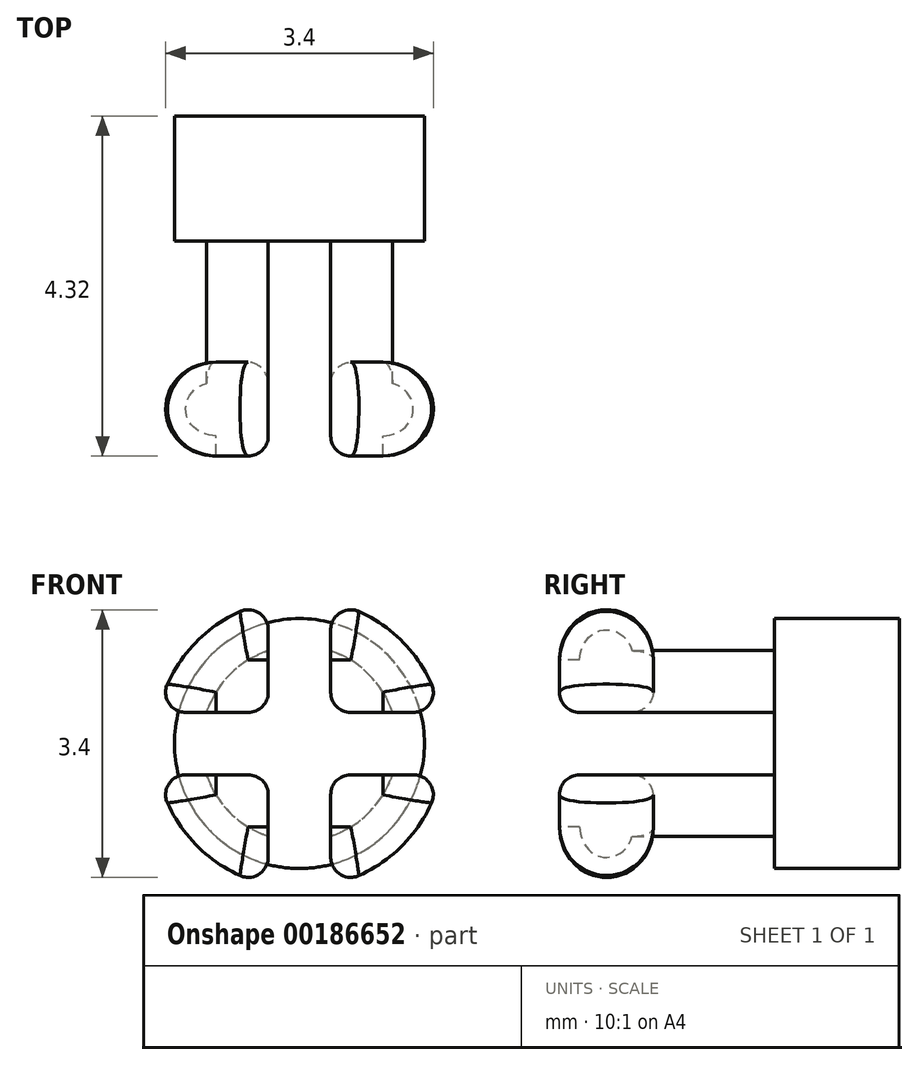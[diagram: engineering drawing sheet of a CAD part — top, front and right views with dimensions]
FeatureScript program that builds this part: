
annotation { "Feature Type Name" : "Feature", "Feature Type Description" : "" }
export const myFeature = defineFeature(function(context is Context, id is Id, definition is map)
    precondition{}
    {
        {
            var Q0;
            Q0=qCreatedBy(makeId("Front.planeOp"),FACE);
            var sketch = newSketch(context, id + "F0", { "sketchPlane" : qUnion([Q0])});
            skCircle(sketch, "E0", {"center": v(0, 0) * mm, "radius": 1.59 * mm});
            skSolve(sketch);
        }
        {
            var Q0;
            Q0=makeQuery(id+"F0.imprint","IMPRINT",FACE,{"disambiguationData":[TD([[makeQuery(id+"F0.imprint","IMPRINT",EDGE,{"derivedFrom":sQuery(id+"F0.wireOp",EDGE,"E0")}),1.0]])]});
            extrude(context, id + "F1", {"entities" : qUnion([Q0]), "depth" : 1.59 * mm});
        }
        {
            var Q0;
            Q0=makeQuery(id+"F1.opExtrude","CAP_FACE",FACE,{"disambiguationData":[OSD([sQuery(id+"F0.wireOp",EDGE,"E0")])],"isStart":false});
            var sketch = newSketch(context, id + "F2", { "sketchPlane" : qUnion([Q0])});
            skCircle(sketch, "E1", {"center": v(0, 0) * mm, "radius": 1.24 * mm});
            skSolve(sketch);
        }
        {
            var Q0;
            Q0=makeQuery(id+"F2.imprint","IMPRINT",FACE,{"disambiguationData":[TD([[makeQuery(id+"F2.imprint","IMPRINT",EDGE,{"derivedFrom":sQuery(id+"F2.wireOp",EDGE,"E1")}),1.0]])]});
            extrude(context, id + "F3", {"entities" : qUnion([Q0]), "operationType" : NewBodyOperationType.ADD, "depth" : 2.73 * mm});
        }
        {
            var Q0;
            Q0=qCreatedBy(makeId("Right.planeOp"),FACE);
            var sketch = newSketch(context, id + "F4", { "sketchPlane" : qUnion([Q0])});
            skLineSegment(sketch, "E2.bottom", {"start": v(-4.32, 0) * mm, "end": v(-3.12, 0) * mm, "construction": true});
            skLineSegment(sketch, "E2.top", {"start": v(-4.32, -1.24) * mm, "end": v(-3.12, -1.24) * mm, "construction": true});
            skLineSegment(sketch, "E2.left", {"start": v(-4.32, 0) * mm, "end": v(-4.32, -1.24) * mm, "construction": true});
            skLineSegment(sketch, "E2.right", {"start": v(-3.12, 0) * mm, "end": v(-3.12, -1.24) * mm, "construction": true});
            skArc(sketch, "E3", {"start": v(-4.32, -1.24) * mm, "mid": v(-3.72, -1.84) * mm, "end": v(-3.12, -1.24) * mm});
            skLineSegment(sketch, "E4", {"start": v(-4.32, -1.24) * mm, "end": v(-3.12, -1.24) * mm});
            skSolve(sketch);
        }
        {
            var Q0;
            Q0 = qSketchRegion(id + "F4", true);
            var Q1;
            Q1=sQuery(id+"F4.wireOp",EDGE,"E2.bottom");
            revolve(context, id + "F5", {"operationType" : NewBodyOperationType.ADD, "entities" : qUnion([Q0]), "axis" : qUnion([Q1]), "revolveType" : RevolveType.FULL});
        }
        {
            var Q0;
            Q0=makeQuery(id+"F3.opExtrude","CAP_FACE",FACE,{"disambiguationData":[OSD([sQuery(id+"F2.wireOp",EDGE,"E1")])],"isStart":false});
            var sketch = newSketch(context, id + "F6", { "sketchPlane" : qUnion([Q0])});
            skLineSegment(sketch, "E5.bottom", {"start": v(0.4, 2.76) * mm, "end": v(-0.4, 2.76) * mm});
            skLineSegment(sketch, "E5.top", {"start": v(0.4, -2.76) * mm, "end": v(-0.4, -2.76) * mm});
            skLineSegment(sketch, "E5.left", {"start": v(0.4, 2.76) * mm, "end": v(0.4, -2.76) * mm});
            skLineSegment(sketch, "E5.right", {"start": v(-0.4, 2.76) * mm, "end": v(-0.4, -2.76) * mm});
            skPoint(sketch, "E5.middle", {"position": v(0, 0) * mm});
            skLineSegment(sketch, "E6.bottom", {"start": v(2.76, -0.4) * mm, "end": v(-2.76, -0.4) * mm});
            skLineSegment(sketch, "E6.top", {"start": v(2.76, 0.4) * mm, "end": v(-2.76, 0.4) * mm});
            skLineSegment(sketch, "E6.left", {"start": v(2.76, -0.4) * mm, "end": v(2.76, 0.4) * mm});
            skLineSegment(sketch, "E6.right", {"start": v(-2.76, -0.4) * mm, "end": v(-2.76, 0.4) * mm});
            skSolve(sketch);
        }
        {
            var Q0;
            {var subQ0=sQuery(id+"F6.wireOp",EDGE,"E5.bottom");Q0=makeQuery(id+"F6.imprint","IMPRINT",FACE,{"disambiguationData":[TD([[makeQuery(id+"F6.imprint","IMPRINT",EDGE,{"derivedFrom":subQ0}),1.0]])]});}
            var Q1;
            {var subQ0=sQuery(id+"F6.wireOp",EDGE,"E6.top");var subQ1=sQuery(id+"F6.wireOp",EDGE,"E5.left");var subQ2=makeQuery(id+"F6.imprint","INTERSECT",VERTEX,{"derivedFrom":[subQ1,subQ0]});Q1=makeQuery(id+"F6.imprint","IMPRINT",FACE,{"disambiguationData":[TD([[makeQuery(id+"F6.imprint","IMPRINT",EDGE,{"disambiguationData":[TD([[subQ2,-1.0]])],"derivedFrom":subQ0}),-1.0]])]});}
            var Q2;
            {var subQ0=sQuery(id+"F6.wireOp",EDGE,"E6.top");var subQ1=sQuery(id+"F6.wireOp",EDGE,"E5.left");var subQ2=makeQuery(id+"F6.imprint","INTERSECT",VERTEX,{"derivedFrom":[subQ1,subQ0]});Q2=makeQuery(id+"F6.imprint","IMPRINT",FACE,{"disambiguationData":[TD([[makeQuery(id+"F6.imprint","IMPRINT",EDGE,{"disambiguationData":[TD([[subQ2,-1.0]])],"derivedFrom":subQ1}),-1.0]])]});}
            var Q3;
            {var subQ0=sQuery(id+"F6.wireOp",EDGE,"E6.bottom");var subQ1=sQuery(id+"F6.wireOp",EDGE,"E5.left");var subQ2=makeQuery(id+"F6.imprint","INTERSECT",VERTEX,{"derivedFrom":[subQ1,subQ0]});Q3=makeQuery(id+"F6.imprint","IMPRINT",FACE,{"disambiguationData":[TD([[makeQuery(id+"F6.imprint","IMPRINT",EDGE,{"disambiguationData":[TD([[subQ2,-1.0]])],"derivedFrom":subQ0}),1.0]])]});}
            var Q4;
            {var subQ0=sQuery(id+"F6.wireOp",EDGE,"E5.top");Q4=makeQuery(id+"F6.imprint","IMPRINT",FACE,{"disambiguationData":[TD([[makeQuery(id+"F6.imprint","IMPRINT",EDGE,{"derivedFrom":subQ0}),-1.0]])]});}
            var Q5;
            {var subQ0=sQuery(id+"F6.wireOp",EDGE,"E6.left");Q5=makeQuery(id+"F6.imprint","IMPRINT",FACE,{"disambiguationData":[TD([[makeQuery(id+"F6.imprint","IMPRINT",EDGE,{"derivedFrom":subQ0}),1.0]])]});}
            var Q6;
            {var subQ0=sQuery(id+"F6.wireOp",EDGE,"E6.top");var subQ1=sQuery(id+"F6.wireOp",EDGE,"E5.left");var subQ2=makeQuery(id+"F6.imprint","INTERSECT",VERTEX,{"derivedFrom":[subQ1,subQ0]});Q6=makeQuery(id+"F6.imprint","IMPRINT",FACE,{"disambiguationData":[TD([[makeQuery(id+"F6.imprint","IMPRINT",EDGE,{"disambiguationData":[TD([[subQ2,-1.0]])],"derivedFrom":subQ1}),1.0]])]});}
            var Q7;
            {var subQ0=sQuery(id+"F6.wireOp",EDGE,"E6.top");var subQ1=sQuery(id+"F6.wireOp",EDGE,"E5.right");var subQ2=makeQuery(id+"F6.imprint","INTERSECT",VERTEX,{"derivedFrom":[subQ1,subQ0]});Q7=makeQuery(id+"F6.imprint","IMPRINT",FACE,{"disambiguationData":[TD([[makeQuery(id+"F6.imprint","IMPRINT",EDGE,{"disambiguationData":[TD([[subQ2,-1.0]])],"derivedFrom":subQ1}),-1.0]])]});}
            var Q8;
            {var subQ0=sQuery(id+"F6.wireOp",EDGE,"E6.right");Q8=makeQuery(id+"F6.imprint","IMPRINT",FACE,{"disambiguationData":[TD([[makeQuery(id+"F6.imprint","IMPRINT",EDGE,{"derivedFrom":subQ0}),-1.0]])]});}
            var Q9;
            Q9=makeQuery(id+"F1.opExtrude","CAP_FACE",FACE,{"disambiguationData":[OSD([sQuery(id+"F0.wireOp",EDGE,"E0")])],"isStart":false});
            extrude(context, id + "F7", {"entities" : qUnion([Q0, Q1, Q2, Q3, Q4, Q5, Q6, Q7, Q8]), "operationType" : NewBodyOperationType.REMOVE, "endBound" : BoundingType.UP_TO_SURFACE, "oppositeDirection" : true, "endBoundEntityFace" : qUnion([Q9]), "depth" : 25.4 * mm});
        }
        {
            var Q0;
            {var subQ1=sQuery(id+"F4.wireOp",EDGE,"E3");var subQ2=sQuery(id+"F6.wireOp",EDGE,"E6.top");var subQ3=sQuery(id+"F6.wireOp",EDGE,"E5.left");var subQ4=makeQuery(id+"F6.imprint","INTERSECT",VERTEX,{"derivedFrom":[subQ3,subQ2]});var subQ5=sQuery(id+"F4.wireOp",EDGE,"E4");Q0=makeQuery(id+"F7.boolean.opBoolean","SPLIT",EDGE,{"disambiguationData":[TD([makeQuery(id+"F7.opExtrude","SWEPT_FACE",FACE,{"disambiguationData":[OSD([subQ3]),TDD([makeQuery(id+"F6.imprint","IMPRINT",EDGE,{"disambiguationData":[TD([[makeQuery(id+"F6.imprint","INTERSECT",VERTEX,{"derivedFrom":[sQuery(id+"F6.wireOp",EDGE,"E5.bottom"),subQ3]}),-1.0]])],"derivedFrom":subQ3}),makeQuery(id+"F6.imprint","IMPRINT",EDGE,{"disambiguationData":[TD([[subQ4,1.0]])],"derivedFrom":subQ3})])]})])],"derivedFrom":makeQuery(id+"F5.opRevolve","SWEPT_EDGE",EDGE,{"disambiguationData":[OSD([subQ1,subQ5]),TDD([makeQuery(id+"F4.imprint","INTERSECT",VERTEX,{"disambiguationData":[OD(1.0)],"derivedFrom":[subQ1,subQ5]})])]})});}
            var Q1;
            {var subQ1=sQuery(id+"F4.wireOp",EDGE,"E3");var subQ2=sQuery(id+"F6.wireOp",EDGE,"E6.top");var subQ3=sQuery(id+"F6.wireOp",EDGE,"E5.right");var subQ4=makeQuery(id+"F6.imprint","INTERSECT",VERTEX,{"derivedFrom":[subQ3,subQ2]});var subQ5=sQuery(id+"F4.wireOp",EDGE,"E4");Q1=makeQuery(id+"F7.boolean.opBoolean","SPLIT",EDGE,{"disambiguationData":[TD([makeQuery(id+"F7.opExtrude","SWEPT_FACE",FACE,{"disambiguationData":[OSD([subQ3]),TDD([makeQuery(id+"F6.imprint","IMPRINT",EDGE,{"disambiguationData":[TD([[makeQuery(id+"F6.imprint","INTERSECT",VERTEX,{"derivedFrom":[sQuery(id+"F6.wireOp",EDGE,"E5.bottom"),subQ3]}),-1.0]])],"derivedFrom":subQ3}),makeQuery(id+"F6.imprint","IMPRINT",EDGE,{"disambiguationData":[TD([[subQ4,1.0]])],"derivedFrom":subQ3})])]})])],"derivedFrom":makeQuery(id+"F5.opRevolve","SWEPT_EDGE",EDGE,{"disambiguationData":[OSD([subQ1,subQ5]),TDD([makeQuery(id+"F4.imprint","INTERSECT",VERTEX,{"disambiguationData":[OD(1.0)],"derivedFrom":[subQ1,subQ5]})])]})});}
            var Q2;
            {var subQ1=sQuery(id+"F6.wireOp",EDGE,"E6.bottom");var subQ2=sQuery(id+"F4.wireOp",EDGE,"E4");var subQ3=sQuery(id+"F4.wireOp",EDGE,"E3");var subQ6=sQuery(id+"F6.wireOp",EDGE,"E5.right");var subQ7=makeQuery(id+"F6.imprint","INTERSECT",VERTEX,{"derivedFrom":[subQ6,subQ1]});Q2=makeQuery(id+"F7.boolean.opBoolean","SPLIT",EDGE,{"disambiguationData":[TD([makeQuery(id+"F7.opExtrude","SWEPT_FACE",FACE,{"disambiguationData":[OSD([subQ6]),TDD([makeQuery(id+"F6.imprint","IMPRINT",EDGE,{"disambiguationData":[TD([[subQ7,-1.0]])],"derivedFrom":subQ6}),makeQuery(id+"F6.imprint","IMPRINT",EDGE,{"disambiguationData":[TD([[makeQuery(id+"F6.imprint","INTERSECT",VERTEX,{"derivedFrom":[sQuery(id+"F6.wireOp",EDGE,"E5.top"),subQ6]}),1.0]])],"derivedFrom":subQ6})])]})])],"derivedFrom":makeQuery(id+"F5.opRevolve","SWEPT_EDGE",EDGE,{"disambiguationData":[OSD([subQ3,subQ2]),TDD([makeQuery(id+"F4.imprint","INTERSECT",VERTEX,{"disambiguationData":[OD(1.0)],"derivedFrom":[subQ3,subQ2]})])]})});}
            var Q3;
            {var subQ1=sQuery(id+"F4.wireOp",EDGE,"E3");var subQ2=sQuery(id+"F6.wireOp",EDGE,"E5.left");var subQ3=sQuery(id+"F4.wireOp",EDGE,"E4");var subQ6=sQuery(id+"F6.wireOp",EDGE,"E6.bottom");var subQ7=makeQuery(id+"F6.imprint","INTERSECT",VERTEX,{"derivedFrom":[subQ2,subQ6]});Q3=makeQuery(id+"F7.boolean.opBoolean","SPLIT",EDGE,{"disambiguationData":[TD([makeQuery(id+"F7.opExtrude","SWEPT_FACE",FACE,{"disambiguationData":[OSD([subQ2]),TDD([makeQuery(id+"F6.imprint","IMPRINT",EDGE,{"disambiguationData":[TD([[subQ7,-1.0]])],"derivedFrom":subQ2}),makeQuery(id+"F6.imprint","IMPRINT",EDGE,{"disambiguationData":[TD([[makeQuery(id+"F6.imprint","INTERSECT",VERTEX,{"derivedFrom":[sQuery(id+"F6.wireOp",EDGE,"E5.top"),subQ2]}),1.0]])],"derivedFrom":subQ2})])]})])],"derivedFrom":makeQuery(id+"F5.opRevolve","SWEPT_EDGE",EDGE,{"disambiguationData":[OSD([subQ1,subQ3]),TDD([makeQuery(id+"F4.imprint","INTERSECT",VERTEX,{"disambiguationData":[OD(1.0)],"derivedFrom":[subQ1,subQ3]})])]})});}
            var Q4;
            {var subQ0=sQuery(id+"F6.wireOp",EDGE,"E5.right");var subQ3=sQuery(id+"F2.wireOp",EDGE,"E1");var subQ6=sQuery(id+"F6.wireOp",EDGE,"E6.bottom");var subQ7=makeQuery(id+"F6.imprint","INTERSECT",VERTEX,{"derivedFrom":[subQ0,subQ6]});Q4=makeQuery(id+"F7.boolean.opBoolean","SPLIT",EDGE,{"disambiguationData":[TD([makeQuery(id+"F7.opExtrude","SWEPT_FACE",FACE,{"disambiguationData":[OSD([subQ0]),TDD([makeQuery(id+"F6.imprint","IMPRINT",EDGE,{"disambiguationData":[TD([[subQ7,-1.0]])],"derivedFrom":subQ0}),makeQuery(id+"F6.imprint","IMPRINT",EDGE,{"disambiguationData":[TD([[makeQuery(id+"F6.imprint","INTERSECT",VERTEX,{"derivedFrom":[sQuery(id+"F6.wireOp",EDGE,"E5.top"),subQ0]}),1.0]])],"derivedFrom":subQ0})])]})])],"derivedFrom":makeQuery(id+"F3.opExtrude","CAP_EDGE",EDGE,{"disambiguationData":[OSD([subQ3])],"isStart":true})});}
            var Q5;
            {var subQ0=sQuery(id+"F6.wireOp",EDGE,"E5.left");var subQ3=sQuery(id+"F2.wireOp",EDGE,"E1");var subQ6=sQuery(id+"F6.wireOp",EDGE,"E6.bottom");var subQ7=makeQuery(id+"F6.imprint","INTERSECT",VERTEX,{"derivedFrom":[subQ0,subQ6]});Q5=makeQuery(id+"F7.boolean.opBoolean","SPLIT",EDGE,{"disambiguationData":[TD([makeQuery(id+"F7.opExtrude","SWEPT_FACE",FACE,{"disambiguationData":[OSD([subQ0]),TDD([makeQuery(id+"F6.imprint","IMPRINT",EDGE,{"disambiguationData":[TD([[subQ7,-1.0]])],"derivedFrom":subQ0}),makeQuery(id+"F6.imprint","IMPRINT",EDGE,{"disambiguationData":[TD([[makeQuery(id+"F6.imprint","INTERSECT",VERTEX,{"derivedFrom":[sQuery(id+"F6.wireOp",EDGE,"E5.top"),subQ0]}),1.0]])],"derivedFrom":subQ0})])]})])],"derivedFrom":makeQuery(id+"F3.opExtrude","CAP_EDGE",EDGE,{"disambiguationData":[OSD([subQ3])],"isStart":true})});}
            var Q6;
            {var subQ0=sQuery(id+"F6.wireOp",EDGE,"E6.top");var subQ1=sQuery(id+"F6.wireOp",EDGE,"E5.left");var subQ2=makeQuery(id+"F6.imprint","INTERSECT",VERTEX,{"derivedFrom":[subQ1,subQ0]});var subQ5=sQuery(id+"F2.wireOp",EDGE,"E1");Q6=makeQuery(id+"F7.boolean.opBoolean","SPLIT",EDGE,{"disambiguationData":[TD([makeQuery(id+"F7.opExtrude","SWEPT_FACE",FACE,{"disambiguationData":[OSD([subQ1]),TDD([makeQuery(id+"F6.imprint","IMPRINT",EDGE,{"disambiguationData":[TD([[makeQuery(id+"F6.imprint","INTERSECT",VERTEX,{"derivedFrom":[sQuery(id+"F6.wireOp",EDGE,"E5.bottom"),subQ1]}),-1.0]])],"derivedFrom":subQ1}),makeQuery(id+"F6.imprint","IMPRINT",EDGE,{"disambiguationData":[TD([[subQ2,1.0]])],"derivedFrom":subQ1})])]})])],"derivedFrom":makeQuery(id+"F3.opExtrude","CAP_EDGE",EDGE,{"disambiguationData":[OSD([subQ5])],"isStart":true})});}
            var Q7;
            {var subQ1=sQuery(id+"F2.wireOp",EDGE,"E1");var subQ2=sQuery(id+"F6.wireOp",EDGE,"E6.top");var subQ3=sQuery(id+"F6.wireOp",EDGE,"E5.right");var subQ4=makeQuery(id+"F6.imprint","INTERSECT",VERTEX,{"derivedFrom":[subQ3,subQ2]});Q7=makeQuery(id+"F7.boolean.opBoolean","SPLIT",EDGE,{"disambiguationData":[TD([makeQuery(id+"F7.opExtrude","SWEPT_FACE",FACE,{"disambiguationData":[OSD([subQ3]),TDD([makeQuery(id+"F6.imprint","IMPRINT",EDGE,{"disambiguationData":[TD([[makeQuery(id+"F6.imprint","INTERSECT",VERTEX,{"derivedFrom":[sQuery(id+"F6.wireOp",EDGE,"E5.bottom"),subQ3]}),-1.0]])],"derivedFrom":subQ3}),makeQuery(id+"F6.imprint","IMPRINT",EDGE,{"disambiguationData":[TD([[subQ4,1.0]])],"derivedFrom":subQ3})])]})])],"derivedFrom":makeQuery(id+"F3.opExtrude","CAP_EDGE",EDGE,{"disambiguationData":[OSD([subQ1])],"isStart":true})});}
            var Q8;
            {var subQ0=sQuery(id+"F6.wireOp",EDGE,"E5.right");Q8=makeQuery(id+"F7.boolean.opBoolean","COPY",EDGE,{"derivedFrom":makeQuery(id+"F7.opExtrude","TWEAK_EDGE",EDGE,{"derivedFrom":[makeQuery(id+"F1.opExtrude","CAP_FACE",FACE,{"disambiguationData":[OSD([sQuery(id+"F0.wireOp",EDGE,"E0")])],"isStart":false}),makeQuery(id+"F6.imprint","IMPRINT",EDGE,{"disambiguationData":[TD([[makeQuery(id+"F6.imprint","INTERSECT",VERTEX,{"derivedFrom":[sQuery(id+"F6.wireOp",EDGE,"E5.bottom"),subQ0]}),-1.0]])],"derivedFrom":subQ0}),makeQuery(id+"F6.imprint","IMPRINT",EDGE,{"disambiguationData":[TD([[makeQuery(id+"F6.imprint","INTERSECT",VERTEX,{"derivedFrom":[subQ0,sQuery(id+"F6.wireOp",EDGE,"E6.top")]}),1.0]])],"derivedFrom":subQ0})]})});}
            var Q9;
            {var subQ0=sQuery(id+"F6.wireOp",EDGE,"E6.bottom");Q9=makeQuery(id+"F7.boolean.opBoolean","COPY",EDGE,{"derivedFrom":makeQuery(id+"F7.opExtrude","TWEAK_EDGE",EDGE,{"derivedFrom":[makeQuery(id+"F1.opExtrude","CAP_FACE",FACE,{"disambiguationData":[OSD([sQuery(id+"F0.wireOp",EDGE,"E0")])],"isStart":false}),makeQuery(id+"F6.imprint","IMPRINT",EDGE,{"disambiguationData":[TD([[makeQuery(id+"F6.imprint","INTERSECT",VERTEX,{"derivedFrom":[subQ0,sQuery(id+"F6.wireOp",EDGE,"E6.left")]}),-1.0]])],"derivedFrom":subQ0}),makeQuery(id+"F6.imprint","IMPRINT",EDGE,{"disambiguationData":[TD([[makeQuery(id+"F6.imprint","INTERSECT",VERTEX,{"derivedFrom":[sQuery(id+"F6.wireOp",EDGE,"E5.left"),subQ0]}),1.0]])],"derivedFrom":subQ0})]})});}
            var Q10;
            {var subQ0=sQuery(id+"F6.wireOp",EDGE,"E5.left");Q10=makeQuery(id+"F7.boolean.opBoolean","COPY",EDGE,{"derivedFrom":makeQuery(id+"F7.opExtrude","TWEAK_EDGE",EDGE,{"derivedFrom":[makeQuery(id+"F1.opExtrude","CAP_FACE",FACE,{"disambiguationData":[OSD([sQuery(id+"F0.wireOp",EDGE,"E0")])],"isStart":false}),makeQuery(id+"F6.imprint","IMPRINT",EDGE,{"disambiguationData":[TD([[makeQuery(id+"F6.imprint","INTERSECT",VERTEX,{"derivedFrom":[sQuery(id+"F6.wireOp",EDGE,"E5.bottom"),subQ0]}),-1.0]])],"derivedFrom":subQ0}),makeQuery(id+"F6.imprint","IMPRINT",EDGE,{"disambiguationData":[TD([[makeQuery(id+"F6.imprint","INTERSECT",VERTEX,{"derivedFrom":[subQ0,sQuery(id+"F6.wireOp",EDGE,"E6.top")]}),1.0]])],"derivedFrom":subQ0})]})});}
            var Q11;
            {var subQ0=sQuery(id+"F6.wireOp",EDGE,"E5.left");Q11=makeQuery(id+"F7.boolean.opBoolean","COPY",EDGE,{"derivedFrom":makeQuery(id+"F7.opExtrude","TWEAK_EDGE",EDGE,{"derivedFrom":[makeQuery(id+"F1.opExtrude","CAP_FACE",FACE,{"disambiguationData":[OSD([sQuery(id+"F0.wireOp",EDGE,"E0")])],"isStart":false}),makeQuery(id+"F6.imprint","IMPRINT",EDGE,{"disambiguationData":[TD([[makeQuery(id+"F6.imprint","INTERSECT",VERTEX,{"derivedFrom":[subQ0,sQuery(id+"F6.wireOp",EDGE,"E6.bottom")]}),-1.0]])],"derivedFrom":subQ0}),makeQuery(id+"F6.imprint","IMPRINT",EDGE,{"disambiguationData":[TD([[makeQuery(id+"F6.imprint","INTERSECT",VERTEX,{"derivedFrom":[sQuery(id+"F6.wireOp",EDGE,"E5.top"),subQ0]}),1.0]])],"derivedFrom":subQ0})]})});}
            var Q12;
            {var subQ0=sQuery(id+"F6.wireOp",EDGE,"E6.bottom");Q12=makeQuery(id+"F7.boolean.opBoolean","COPY",EDGE,{"derivedFrom":makeQuery(id+"F7.opExtrude","TWEAK_EDGE",EDGE,{"derivedFrom":[makeQuery(id+"F1.opExtrude","CAP_FACE",FACE,{"disambiguationData":[OSD([sQuery(id+"F0.wireOp",EDGE,"E0")])],"isStart":false}),makeQuery(id+"F6.imprint","IMPRINT",EDGE,{"disambiguationData":[TD([[makeQuery(id+"F6.imprint","INTERSECT",VERTEX,{"derivedFrom":[sQuery(id+"F6.wireOp",EDGE,"E5.right"),subQ0]}),-1.0]])],"derivedFrom":subQ0}),makeQuery(id+"F6.imprint","IMPRINT",EDGE,{"disambiguationData":[TD([[makeQuery(id+"F6.imprint","INTERSECT",VERTEX,{"derivedFrom":[subQ0,sQuery(id+"F6.wireOp",EDGE,"E6.right")]}),1.0]])],"derivedFrom":subQ0})]})});}
            var Q13;
            {var subQ0=sQuery(id+"F6.wireOp",EDGE,"E6.top");var subQ2=sQuery(id+"F4.wireOp",EDGE,"E3");Q13=makeQuery(id+"F7.boolean.opBoolean","INTERSECT",EDGE,{"derivedFrom":[makeQuery(id+"F5.opRevolve","SWEPT_FACE",FACE,{"disambiguationData":[OSD([subQ2])]}),makeQuery(id+"F7.opExtrude","SWEPT_FACE",FACE,{"disambiguationData":[OSD([subQ0]),TDD([makeQuery(id+"F6.imprint","IMPRINT",EDGE,{"disambiguationData":[TD([[makeQuery(id+"F6.imprint","INTERSECT",VERTEX,{"derivedFrom":[sQuery(id+"F6.wireOp",EDGE,"E5.right"),subQ0]}),-1.0]])],"derivedFrom":subQ0}),makeQuery(id+"F6.imprint","IMPRINT",EDGE,{"disambiguationData":[TD([[makeQuery(id+"F6.imprint","INTERSECT",VERTEX,{"derivedFrom":[subQ0,sQuery(id+"F6.wireOp",EDGE,"E6.right")]}),1.0]])],"derivedFrom":subQ0})])]})]});}
            var Q14;
            {var subQ0=sQuery(id+"F6.wireOp",EDGE,"E6.bottom");var subQ2=sQuery(id+"F4.wireOp",EDGE,"E3");Q14=makeQuery(id+"F7.boolean.opBoolean","INTERSECT",EDGE,{"derivedFrom":[makeQuery(id+"F5.opRevolve","SWEPT_FACE",FACE,{"disambiguationData":[OSD([subQ2])]}),makeQuery(id+"F7.opExtrude","SWEPT_FACE",FACE,{"disambiguationData":[OSD([subQ0]),TDD([makeQuery(id+"F6.imprint","IMPRINT",EDGE,{"disambiguationData":[TD([[makeQuery(id+"F6.imprint","INTERSECT",VERTEX,{"derivedFrom":[sQuery(id+"F6.wireOp",EDGE,"E5.right"),subQ0]}),-1.0]])],"derivedFrom":subQ0}),makeQuery(id+"F6.imprint","IMPRINT",EDGE,{"disambiguationData":[TD([[makeQuery(id+"F6.imprint","INTERSECT",VERTEX,{"derivedFrom":[subQ0,sQuery(id+"F6.wireOp",EDGE,"E6.right")]}),1.0]])],"derivedFrom":subQ0})])]})]});}
            var Q15;
            Q15=makeQuery(id+"F7.boolean.opBoolean","COPY",EDGE,{"derivedFrom":makeQuery(id+"F7.opExtrude","SWEPT_EDGE",EDGE,{"disambiguationData":[OSD([sQuery(id+"F6.wireOp",EDGE,"E5.right"),sQuery(id+"F6.wireOp",EDGE,"E6.bottom")])]})});
            var Q16;
            {var subQ0=sQuery(id+"F6.wireOp",EDGE,"E5.right");var subQ2=sQuery(id+"F4.wireOp",EDGE,"E3");Q16=makeQuery(id+"F7.boolean.opBoolean","INTERSECT",EDGE,{"derivedFrom":[makeQuery(id+"F5.opRevolve","SWEPT_FACE",FACE,{"disambiguationData":[OSD([subQ2])]}),makeQuery(id+"F7.opExtrude","SWEPT_FACE",FACE,{"disambiguationData":[OSD([subQ0]),TDD([makeQuery(id+"F6.imprint","IMPRINT",EDGE,{"disambiguationData":[TD([[makeQuery(id+"F6.imprint","INTERSECT",VERTEX,{"derivedFrom":[subQ0,sQuery(id+"F6.wireOp",EDGE,"E6.bottom")]}),-1.0]])],"derivedFrom":subQ0}),makeQuery(id+"F6.imprint","IMPRINT",EDGE,{"disambiguationData":[TD([[makeQuery(id+"F6.imprint","INTERSECT",VERTEX,{"derivedFrom":[sQuery(id+"F6.wireOp",EDGE,"E5.top"),subQ0]}),1.0]])],"derivedFrom":subQ0})])]})]});}
            var Q17;
            {var subQ0=sQuery(id+"F6.wireOp",EDGE,"E5.right");var subQ2=sQuery(id+"F4.wireOp",EDGE,"E3");Q17=makeQuery(id+"F7.boolean.opBoolean","INTERSECT",EDGE,{"derivedFrom":[makeQuery(id+"F5.opRevolve","SWEPT_FACE",FACE,{"disambiguationData":[OSD([subQ2])]}),makeQuery(id+"F7.opExtrude","SWEPT_FACE",FACE,{"disambiguationData":[OSD([subQ0]),TDD([makeQuery(id+"F6.imprint","IMPRINT",EDGE,{"disambiguationData":[TD([[makeQuery(id+"F6.imprint","INTERSECT",VERTEX,{"derivedFrom":[sQuery(id+"F6.wireOp",EDGE,"E5.bottom"),subQ0]}),-1.0]])],"derivedFrom":subQ0}),makeQuery(id+"F6.imprint","IMPRINT",EDGE,{"disambiguationData":[TD([[makeQuery(id+"F6.imprint","INTERSECT",VERTEX,{"derivedFrom":[subQ0,sQuery(id+"F6.wireOp",EDGE,"E6.top")]}),1.0]])],"derivedFrom":subQ0})])]})]});}
            var Q18;
            {var subQ0=sQuery(id+"F6.wireOp",EDGE,"E6.top");Q18=makeQuery(id+"F7.boolean.opBoolean","COPY",EDGE,{"derivedFrom":makeQuery(id+"F7.opExtrude","CAP_EDGE",EDGE,{"disambiguationData":[OSD([subQ0]),TDD([makeQuery(id+"F6.imprint","IMPRINT",EDGE,{"disambiguationData":[TD([[makeQuery(id+"F6.imprint","INTERSECT",VERTEX,{"derivedFrom":[subQ0,sQuery(id+"F6.wireOp",EDGE,"E6.left")]}),-1.0]])],"derivedFrom":subQ0}),makeQuery(id+"F6.imprint","IMPRINT",EDGE,{"disambiguationData":[TD([[makeQuery(id+"F6.imprint","INTERSECT",VERTEX,{"derivedFrom":[sQuery(id+"F6.wireOp",EDGE,"E5.left"),subQ0]}),1.0]])],"derivedFrom":subQ0})])],"isStart":true})});}
            var Q19;
            {var subQ0=sQuery(id+"F6.wireOp",EDGE,"E5.left");var subQ2=sQuery(id+"F4.wireOp",EDGE,"E3");Q19=makeQuery(id+"F7.boolean.opBoolean","INTERSECT",EDGE,{"derivedFrom":[makeQuery(id+"F5.opRevolve","SWEPT_FACE",FACE,{"disambiguationData":[OSD([subQ2])]}),makeQuery(id+"F7.opExtrude","SWEPT_FACE",FACE,{"disambiguationData":[OSD([subQ0]),TDD([makeQuery(id+"F6.imprint","IMPRINT",EDGE,{"disambiguationData":[TD([[makeQuery(id+"F6.imprint","INTERSECT",VERTEX,{"derivedFrom":[sQuery(id+"F6.wireOp",EDGE,"E5.bottom"),subQ0]}),-1.0]])],"derivedFrom":subQ0}),makeQuery(id+"F6.imprint","IMPRINT",EDGE,{"disambiguationData":[TD([[makeQuery(id+"F6.imprint","INTERSECT",VERTEX,{"derivedFrom":[subQ0,sQuery(id+"F6.wireOp",EDGE,"E6.top")]}),1.0]])],"derivedFrom":subQ0})])]})]});}
            var Q20;
            {var subQ0=sQuery(id+"F6.wireOp",EDGE,"E6.bottom");var subQ2=sQuery(id+"F4.wireOp",EDGE,"E3");Q20=makeQuery(id+"F7.boolean.opBoolean","INTERSECT",EDGE,{"derivedFrom":[makeQuery(id+"F5.opRevolve","SWEPT_FACE",FACE,{"disambiguationData":[OSD([subQ2])]}),makeQuery(id+"F7.opExtrude","SWEPT_FACE",FACE,{"disambiguationData":[OSD([subQ0]),TDD([makeQuery(id+"F6.imprint","IMPRINT",EDGE,{"disambiguationData":[TD([[makeQuery(id+"F6.imprint","INTERSECT",VERTEX,{"derivedFrom":[subQ0,sQuery(id+"F6.wireOp",EDGE,"E6.left")]}),-1.0]])],"derivedFrom":subQ0}),makeQuery(id+"F6.imprint","IMPRINT",EDGE,{"disambiguationData":[TD([[makeQuery(id+"F6.imprint","INTERSECT",VERTEX,{"derivedFrom":[sQuery(id+"F6.wireOp",EDGE,"E5.left"),subQ0]}),1.0]])],"derivedFrom":subQ0})])]})]});}
            var Q21;
            {var subQ0=sQuery(id+"F6.wireOp",EDGE,"E5.left");var subQ2=sQuery(id+"F4.wireOp",EDGE,"E3");Q21=makeQuery(id+"F7.boolean.opBoolean","INTERSECT",EDGE,{"derivedFrom":[makeQuery(id+"F5.opRevolve","SWEPT_FACE",FACE,{"disambiguationData":[OSD([subQ2])]}),makeQuery(id+"F7.opExtrude","SWEPT_FACE",FACE,{"disambiguationData":[OSD([subQ0]),TDD([makeQuery(id+"F6.imprint","IMPRINT",EDGE,{"disambiguationData":[TD([[makeQuery(id+"F6.imprint","INTERSECT",VERTEX,{"derivedFrom":[subQ0,sQuery(id+"F6.wireOp",EDGE,"E6.bottom")]}),-1.0]])],"derivedFrom":subQ0}),makeQuery(id+"F6.imprint","IMPRINT",EDGE,{"disambiguationData":[TD([[makeQuery(id+"F6.imprint","INTERSECT",VERTEX,{"derivedFrom":[sQuery(id+"F6.wireOp",EDGE,"E5.top"),subQ0]}),1.0]])],"derivedFrom":subQ0})])]})]});}
            var Q22;
            Q22=makeQuery(id+"F7.boolean.opBoolean","COPY",EDGE,{"derivedFrom":makeQuery(id+"F7.opExtrude","SWEPT_EDGE",EDGE,{"disambiguationData":[OSD([sQuery(id+"F6.wireOp",EDGE,"E5.left"),sQuery(id+"F6.wireOp",EDGE,"E6.top")])]})});
            var Q23;
            Q23=makeQuery(id+"F7.boolean.opBoolean","COPY",EDGE,{"derivedFrom":makeQuery(id+"F7.opExtrude","SWEPT_EDGE",EDGE,{"disambiguationData":[OSD([sQuery(id+"F6.wireOp",EDGE,"E5.left"),sQuery(id+"F6.wireOp",EDGE,"E6.bottom")])]})});
            var Q24;
            Q24=makeQuery(id+"F7.boolean.opBoolean","COPY",EDGE,{"derivedFrom":makeQuery(id+"F7.opExtrude","SWEPT_EDGE",EDGE,{"disambiguationData":[OSD([sQuery(id+"F6.wireOp",EDGE,"E5.right"),sQuery(id+"F6.wireOp",EDGE,"E6.top")])]})});
            fillet(context, id + "F8", {"entities" : qUnion([Q0, Q1, Q2, Q3, Q4, Q5, Q6, Q7, Q8, Q9, Q10, Q11, Q12, Q13, Q14, Q15, Q16, Q17, Q18, Q19, Q20, Q21, Q22, Q23, Q24]), "radius" : 0.25 * mm, "tangentPropagation" : true, "allowEdgeOverflow" : false});
        }
    });
